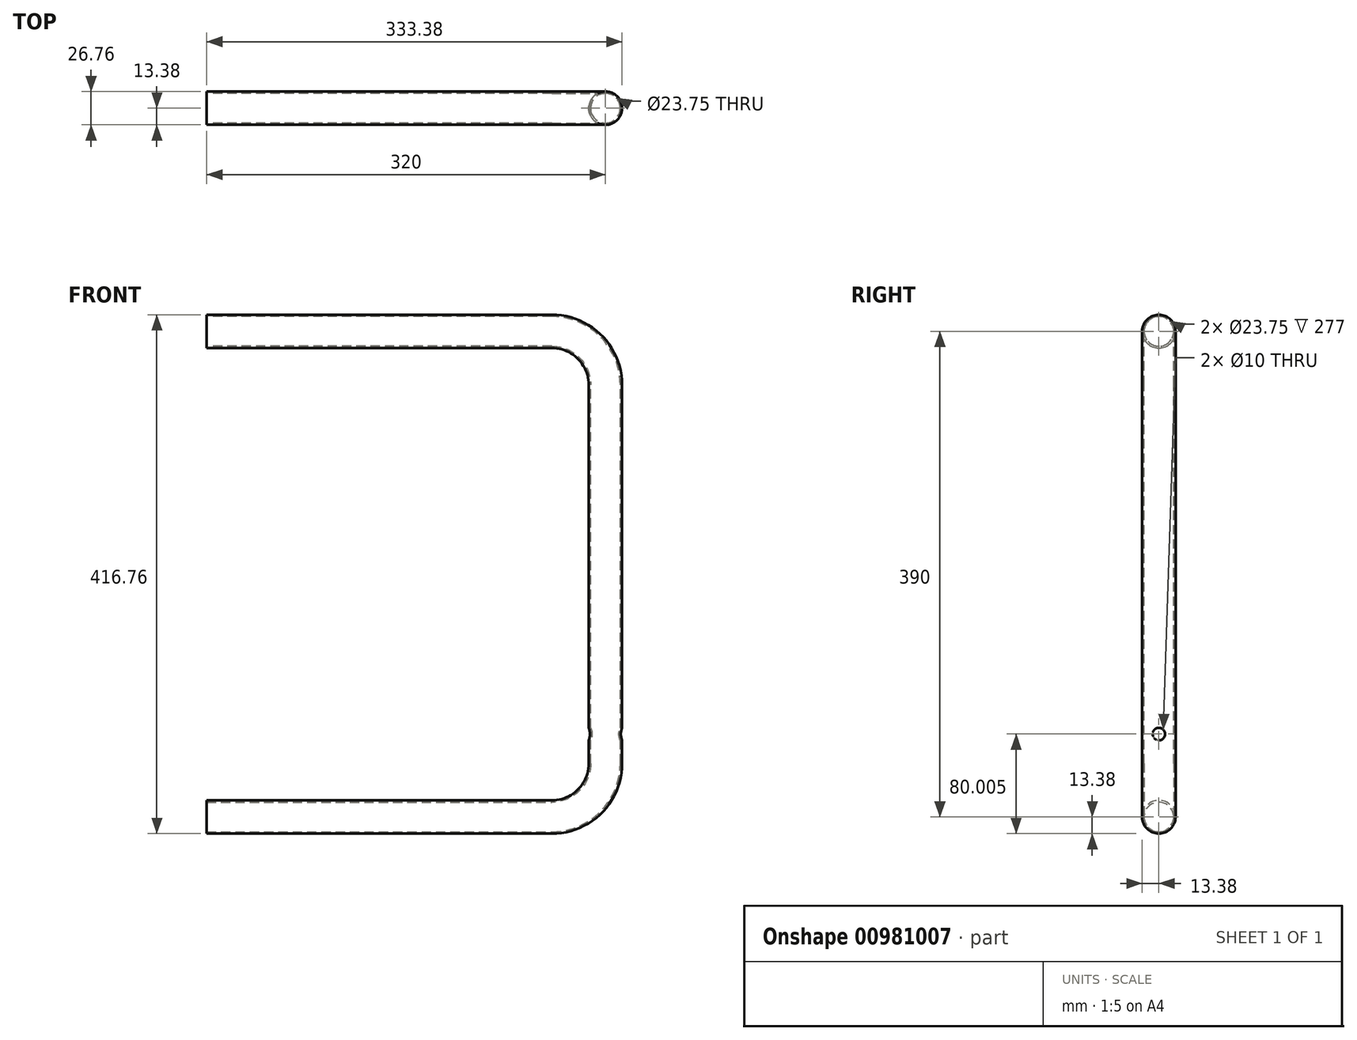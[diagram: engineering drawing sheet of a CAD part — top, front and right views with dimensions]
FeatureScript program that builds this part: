
annotation { "Feature Type Name" : "Feature", "Feature Type Description" : "" }
export const myFeature = defineFeature(function(context is Context, id is Id, definition is map)
    precondition{}
    {
        {
            var Q0;
            Q0=qCreatedBy(makeId("Front.planeOp"),FACE);
            var sketch = newSketch(context, id + "F0", { "sketchPlane" : qUnion([Q0])});
            skLineSegment(sketch, "E0", {"start": v(0, 0) * mm, "end": v(277, 0) * mm});
            skLineSegment(sketch, "E1", {"start": v(320, 43) * mm, "end": v(320, 347) * mm});
            skLineSegment(sketch, "E2", {"start": v(277, 390) * mm, "end": v(0, 390) * mm});
            skPoint(sketch, "E3.visualSharp", {"position": v(320, 0) * mm});
            skArc(sketch, "E3.filletArc", {"start": v(277, 0) * mm, "mid": v(307.4, 12.6) * mm, "end": v(320, 43) * mm});
            skPoint(sketch, "E4.visualSharp", {"position": v(320, 390) * mm});
            skArc(sketch, "E4.filletArc", {"start": v(320, 347) * mm, "mid": v(307.4, 377.4) * mm, "end": v(277, 390) * mm});
            skSolve(sketch);
        }
        {
            var Q0;
            Q0=qCreatedBy(makeId("Right.planeOp"),FACE);
            var sketch = newSketch(context, id + "F1", { "sketchPlane" : qUnion([Q0])});
            skCircle(sketch, "E5", {"center": v(0, 0) * mm, "radius": 13.38 * mm});
            skCircle(sketch, "E6", {"center": v(0, 0) * mm, "radius": 11.88 * mm});
            skSolve(sketch);
        }
        {
            var Q0;
            Q0=makeQuery(id+"F1.imprint","IMPRINT",FACE,{"disambiguationData":[TD([[makeQuery(id+"F1.imprint","IMPRINT",EDGE,{"derivedFrom":sQuery(id+"F1.wireOp",EDGE,"E5")}),1.0]])]});
            var Q1;
            Q1=sQuery(id+"F0.wireOp",EDGE,"E0");
            var Q2;
            Q2=sQuery(id+"F0.wireOp",EDGE,"E3.filletArc");
            var Q3;
            Q3=sQuery(id+"F0.wireOp",EDGE,"E1");
            var Q4;
            Q4=sQuery(id+"F0.wireOp",EDGE,"E4.filletArc");
            var Q5;
            Q5=sQuery(id+"F0.wireOp",EDGE,"E2");
            sweep(context, id + "F2", {"profiles" : qUnion([Q0]), "path" : qUnion([Q1, Q2, Q3, Q4, Q5])});
        }
        {
            var Q0;
            Q0=qCreatedBy(makeId("Right.planeOp"),FACE);
            var sketch = newSketch(context, id + "F3", { "sketchPlane" : qUnion([Q0])});
            skCircle(sketch, "E7", {"center": v(0, 66.62) * mm, "radius": 5 * mm});
            skLineSegment(sketch, "E8", {"start": v(0, 66.62) * mm, "end": v(0, -13.37) * mm, "construction": true});
            skSolve(sketch);
        }
        {
            var Q0;
            Q0 = qSketchRegion(id + "F3", true);
            extrude(context, id + "F4", {"entities" : qUnion([Q0]), "operationType" : NewBodyOperationType.REMOVE, "endBound" : BoundingType.THROUGH_ALL, "depth" : 25 * mm, "offsetDistance" : 25 * mm});
        }
    });
